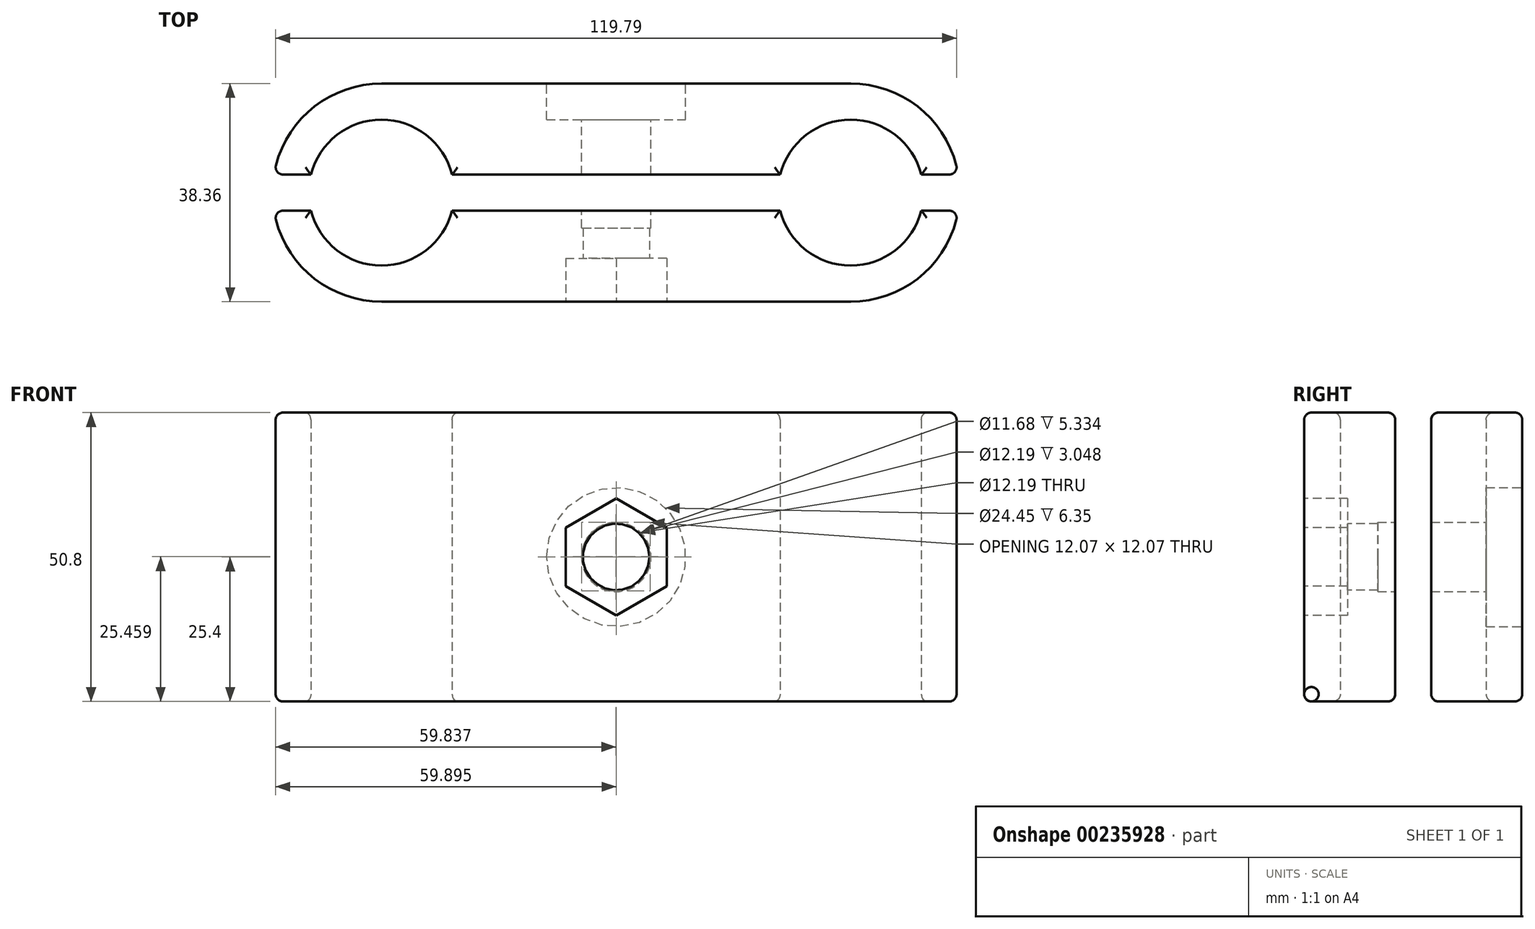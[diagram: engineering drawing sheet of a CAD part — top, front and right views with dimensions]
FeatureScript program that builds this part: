
annotation { "Feature Type Name" : "Feature", "Feature Type Description" : "" }
export const myFeature = defineFeature(function(context is Context, id is Id, definition is map)
    precondition{}
    {
        {
            var Q0;
            Q0=qCreatedBy(makeId("Top.planeOp"),FACE);
            var sketch = newSketch(context, id + "F0", { "sketchPlane" : qUnion([Q0])});
            skArc(sketch, "E0", {"start": v(-12.43, -3.18) * mm, "mid": v(0, -12.83) * mm, "end": v(12.43, -3.17) * mm});
            skArc(sketch, "E1", {"start": v(70.12, -3.17) * mm, "mid": v(82.55, -12.83) * mm, "end": v(94.98, -3.18) * mm});
            skArc(sketch, "E2.0", {"start": v(18.91, 3.17) * mm, "mid": v(0, 19.18) * mm, "end": v(-18.91, 3.17) * mm});
            skArc(sketch, "E3.0", {"start": v(63.64, -3.17) * mm, "mid": v(82.55, -19.18) * mm, "end": v(101.46, -3.18) * mm});
            skLineSegment(sketch, "E4", {"start": v(0, -19.18) * mm, "end": v(82.55, -19.18) * mm});
            skLineSegment(sketch, "E5", {"start": v(0, 19.18) * mm, "end": v(82.55, 19.18) * mm});
            skLineSegment(sketch, "E6.0", {"start": v(-18.91, -3.18) * mm, "end": v(-12.43, -3.18) * mm});
            skLineSegment(sketch, "E7.0", {"start": v(-18.91, 3.18) * mm, "end": v(-12.43, 3.18) * mm});
            skPoint(sketch, "E8.orphan", {"position": v(-19.18, 0) * mm});
            skArc(sketch, "E9.trimOffspring", {"start": v(12.43, 3.17) * mm, "mid": v(0, 12.83) * mm, "end": v(-12.43, 3.18) * mm});
            skArc(sketch, "E10.trimOffspring", {"start": v(94.98, 3.17) * mm, "mid": v(82.55, 12.83) * mm, "end": v(70.12, 3.18) * mm});
            skArc(sketch, "E11.trimOffspring", {"start": v(101.46, 3.18) * mm, "mid": v(82.55, 19.18) * mm, "end": v(63.64, 3.17) * mm});
            skArc(sketch, "E12.trimOffspring", {"start": v(-18.91, -3.17) * mm, "mid": v(0, -19.18) * mm, "end": v(18.91, -3.18) * mm});
            skLineSegment(sketch, "E13.trimOffspring", {"start": v(12.43, -3.18) * mm, "end": v(70.12, -3.18) * mm});
            skLineSegment(sketch, "E14.trimOffspring", {"start": v(12.43, 3.18) * mm, "end": v(70.12, 3.18) * mm});
            skLineSegment(sketch, "E15.trimOffspring", {"start": v(94.98, 3.18) * mm, "end": v(101.46, 3.18) * mm});
            skLineSegment(sketch, "E16.trimOffspring", {"start": v(94.98, -3.18) * mm, "end": v(101.46, -3.18) * mm});
            skSolve(sketch);
        }
        {
            var Q0;
            {var subQ3=sQuery(id+"F0.wireOp",EDGE,"E5");Q0=makeQuery(id+"F0.imprint","IMPRINT",FACE,{"disambiguationData":[TD([[makeQuery(id+"F0.imprint","IMPRINT",EDGE,{"derivedFrom":subQ3}),-1.0]])]});}
            var Q1;
            {var subQ1=sQuery(id+"F0.wireOp",EDGE,"E7.0");Q1=makeQuery(id+"F0.imprint","IMPRINT",FACE,{"disambiguationData":[TD([[makeQuery(id+"F0.imprint","IMPRINT",EDGE,{"derivedFrom":subQ1}),1.0]])]});}
            var Q2;
            {var subQ1=sQuery(id+"F0.wireOp",EDGE,"E10.trimOffspring");Q2=makeQuery(id+"F0.imprint","IMPRINT",FACE,{"disambiguationData":[TD([[makeQuery(id+"F0.imprint","IMPRINT",EDGE,{"derivedFrom":subQ1}),-1.0]])]});}
            var Q3;
            {var subQ3=sQuery(id+"F0.wireOp",EDGE,"E4");Q3=makeQuery(id+"F0.imprint","IMPRINT",FACE,{"disambiguationData":[TD([[makeQuery(id+"F0.imprint","IMPRINT",EDGE,{"derivedFrom":subQ3}),1.0]])]});}
            var Q4;
            {var subQ5=sQuery(id+"F0.wireOp",EDGE,"E1");Q4=makeQuery(id+"F0.imprint","IMPRINT",FACE,{"disambiguationData":[TD([[makeQuery(id+"F0.imprint","IMPRINT",EDGE,{"derivedFrom":subQ5}),-1.0]])]});}
            var Q5;
            {var subQ5=sQuery(id+"F0.wireOp",EDGE,"E0");Q5=makeQuery(id+"F0.imprint","IMPRINT",FACE,{"disambiguationData":[TD([[makeQuery(id+"F0.imprint","IMPRINT",EDGE,{"derivedFrom":subQ5}),-1.0]])]});}
            extrude(context, id + "F1", {"entities" : qUnion([Q0, Q1, Q2, Q3, Q4, Q5]), "depth" : 50.8 * mm});
        }
        {
            var Q0;
            Q0=makeQuery(id+"F1.opExtrude","SWEPT_FACE",FACE,{"disambiguationData":[OSD([sQuery(id+"F0.wireOp",EDGE,"E4")])]});
            var sketch = newSketch(context, id + "F2", { "sketchPlane" : qUnion([Q0])});
            skCircle(sketch, "E17.cCircle", {"center": v(41.28, 25.4) * mm, "radius": 8.9 * mm, "construction": true});
            skPoint(sketch, "E17.cCircle.centerSnap0", {"position": v(41.28, 50.8) * mm});
            skLineSegment(sketch, "E17.0", {"start": v(50.17, 20.27) * mm, "end": v(41.28, 15.13) * mm});
            skLineSegment(sketch, "E17.1", {"start": v(41.28, 15.13) * mm, "end": v(32.39, 20.27) * mm});
            skLineSegment(sketch, "E17.2", {"start": v(32.39, 20.27) * mm, "end": v(32.39, 30.53) * mm});
            skLineSegment(sketch, "E17.3", {"start": v(32.39, 30.53) * mm, "end": v(41.27, 35.67) * mm});
            skLineSegment(sketch, "E17.4", {"start": v(41.27, 35.67) * mm, "end": v(50.17, 30.53) * mm});
            skLineSegment(sketch, "E17.5", {"start": v(50.17, 30.53) * mm, "end": v(50.17, 20.27) * mm});
            skPoint(sketch, "E17.0.midPoint", {"position": v(45.72, 17.7) * mm});
            skCircle(sketch, "E18", {"center": v(41.28, 25.4) * mm, "radius": 5.84 * mm});
            skSolve(sketch);
        }
        {
            var Q0;
            Q0=makeQuery(id+"F2.imprint","IMPRINT",FACE,{"disambiguationData":[TD([[makeQuery(id+"F2.imprint","IMPRINT",EDGE,{"derivedFrom":sQuery(id+"F2.wireOp",EDGE,"E18")}),1.0]])]});
            extrude(context, id + "F3", {"entities" : qUnion([Q0]), "operationType" : NewBodyOperationType.REMOVE, "oppositeDirection" : true, "depth" : 25.4 * mm});
        }
        {
            var Q0;
            Q0=makeQuery(id+"F2.imprint","IMPRINT",FACE,{"disambiguationData":[TD([[makeQuery(id+"F2.imprint","IMPRINT",EDGE,{"derivedFrom":sQuery(id+"F2.wireOp",EDGE,"E17.0")}),-1.0]])]});
            extrude(context, id + "F4", {"entities" : qUnion([Q0]), "operationType" : NewBodyOperationType.REMOVE, "oppositeDirection" : true, "depth" : 7.62 * mm});
        }
        {
            var Q0;
            Q0=makeQuery(id+"F1.opExtrude","SWEPT_FACE",FACE,{"disambiguationData":[OSD([sQuery(id+"F0.wireOp",EDGE,"E5")])]});
            var sketch = newSketch(context, id + "F5", { "sketchPlane" : qUnion([Q0])});
            skCircle(sketch, "E19", {"center": v(-41.28, 25.4) * mm, "radius": 6.1 * mm});
            skPoint(sketch, "E19.centerSnap0", {"position": v(-41.28, 50.8) * mm});
            skCircle(sketch, "E20", {"center": v(-41.28, 25.4) * mm, "radius": 12.23 * mm});
            skSolve(sketch);
        }
        {
            var Q0;
            Q0=makeQuery(id+"F5.imprint","IMPRINT",FACE,{"disambiguationData":[TD([[makeQuery(id+"F5.imprint","IMPRINT",EDGE,{"derivedFrom":sQuery(id+"F5.wireOp",EDGE,"E19")}),1.0]])]});
            extrude(context, id + "F6", {"entities" : qUnion([Q0]), "operationType" : NewBodyOperationType.REMOVE, "oppositeDirection" : true, "depth" : 25.4 * mm});
        }
        {
            var Q0;
            Q0=makeQuery(id+"F5.imprint","IMPRINT",FACE,{"disambiguationData":[TD([[makeQuery(id+"F5.imprint","IMPRINT",EDGE,{"derivedFrom":sQuery(id+"F5.wireOp",EDGE,"E19")}),-1.0]])]});
            extrude(context, id + "F7", {"entities" : qUnion([Q0]), "operationType" : NewBodyOperationType.REMOVE, "oppositeDirection" : true, "depth" : 6.35 * mm});
        }
        {
            var Q0;
            Q0=makeQuery(id+"F1.opExtrude","CAP_FACE",FACE,{"disambiguationData":[OSD([sQuery(id+"F0.wireOp",EDGE,"E0"),sQuery(id+"F0.wireOp",EDGE,"E1"),sQuery(id+"F0.wireOp",EDGE,"E3.0"),sQuery(id+"F0.wireOp",EDGE,"E4"),sQuery(id+"F0.wireOp",EDGE,"E6.0"),sQuery(id+"F0.wireOp",EDGE,"E12.trimOffspring"),sQuery(id+"F0.wireOp",EDGE,"E13.trimOffspring"),sQuery(id+"F0.wireOp",EDGE,"E16.trimOffspring")])],"isStart":false});
            var Q1;
            Q1=makeQuery(id+"F1.opExtrude","CAP_FACE",FACE,{"disambiguationData":[OSD([sQuery(id+"F0.wireOp",EDGE,"E2.0"),sQuery(id+"F0.wireOp",EDGE,"E5"),sQuery(id+"F0.wireOp",EDGE,"E7.0"),sQuery(id+"F0.wireOp",EDGE,"E9.trimOffspring"),sQuery(id+"F0.wireOp",EDGE,"E10.trimOffspring"),sQuery(id+"F0.wireOp",EDGE,"E11.trimOffspring"),sQuery(id+"F0.wireOp",EDGE,"E14.trimOffspring"),sQuery(id+"F0.wireOp",EDGE,"E15.trimOffspring")])],"isStart":false});
            var Q2;
            Q2=makeQuery(id+"F1.opExtrude","CAP_FACE",FACE,{"disambiguationData":[OSD([sQuery(id+"F0.wireOp",EDGE,"E0"),sQuery(id+"F0.wireOp",EDGE,"E1"),sQuery(id+"F0.wireOp",EDGE,"E3.0"),sQuery(id+"F0.wireOp",EDGE,"E4"),sQuery(id+"F0.wireOp",EDGE,"E6.0"),sQuery(id+"F0.wireOp",EDGE,"E12.trimOffspring"),sQuery(id+"F0.wireOp",EDGE,"E13.trimOffspring"),sQuery(id+"F0.wireOp",EDGE,"E16.trimOffspring")])],"isStart":true});
            var Q3;
            Q3=makeQuery(id+"F1.opExtrude","CAP_FACE",FACE,{"disambiguationData":[OSD([sQuery(id+"F0.wireOp",EDGE,"E2.0"),sQuery(id+"F0.wireOp",EDGE,"E5"),sQuery(id+"F0.wireOp",EDGE,"E7.0"),sQuery(id+"F0.wireOp",EDGE,"E9.trimOffspring"),sQuery(id+"F0.wireOp",EDGE,"E10.trimOffspring"),sQuery(id+"F0.wireOp",EDGE,"E11.trimOffspring"),sQuery(id+"F0.wireOp",EDGE,"E14.trimOffspring"),sQuery(id+"F0.wireOp",EDGE,"E15.trimOffspring")])],"isStart":true});
            var Q4;
            Q4=makeQuery(id+"F7.boolean.opBoolean","COPY",EDGE,{"derivedFrom":makeQuery(id+"F7.opExtrude","CAP_EDGE",EDGE,{"disambiguationData":[OSD([sQuery(id+"F5.wireOp",EDGE,"E20")])],"isStart":true})});
            var Q5;
            Q5=makeQuery(id+"F1.opExtrude","SWEPT_EDGE",EDGE,{"disambiguationData":[OSD([sQuery(id+"F0.wireOp",EDGE,"E3.0"),sQuery(id+"F0.wireOp",EDGE,"E16.trimOffspring")])]});
            var Q6;
            Q6=makeQuery(id+"F1.opExtrude","SWEPT_EDGE",EDGE,{"disambiguationData":[OSD([sQuery(id+"F0.wireOp",EDGE,"E11.trimOffspring"),sQuery(id+"F0.wireOp",EDGE,"E15.trimOffspring")])]});
            var Q7;
            Q7=makeQuery(id+"F1.opExtrude","SWEPT_EDGE",EDGE,{"disambiguationData":[OSD([sQuery(id+"F0.wireOp",EDGE,"E2.0"),sQuery(id+"F0.wireOp",EDGE,"E7.0")])]});
            var Q8;
            Q8=makeQuery(id+"F1.opExtrude","SWEPT_EDGE",EDGE,{"disambiguationData":[OSD([sQuery(id+"F0.wireOp",EDGE,"E6.0"),sQuery(id+"F0.wireOp",EDGE,"E12.trimOffspring")])]});
            fillet(context, id + "F8", {"entities" : qUnion([Q0, Q1, Q2, Q3, Q4, Q5, Q6, Q7, Q8]), "radius" : 1.27 * mm, "tangentPropagation" : true, "allowEdgeOverflow" : false});
        }
    });
